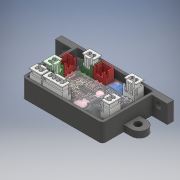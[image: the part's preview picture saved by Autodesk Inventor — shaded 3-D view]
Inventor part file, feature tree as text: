
AUTODESK INVENTOR PART (.ipt)
format: ipt  version: 2017 (Build 210142000, 142)  size: 2,653,696 bytes
history: native  units: mm
features: other x18, sketch x7, extrude x3, fillet x2, hole x2, mirror x1
ambient origin geometry x8: Origin, YZ Plane, XZ Plane, XY Plane, X Axis, Y Axis, Z Axis, Center Point
bodies: Solide10 (feature_tree)
feature tree (33):
  other  "Connecteur jst 2 broches.iam"
  other  "Connecteur jst 4 broches.iam"
  other  "Connecteur jst 2 broches femelle.ipt:1"
  other  "Connecteur JST 2 Broches Male.ipt:1"
  other  "Connecteur jst 4 broches femelle.ipt:1"
  other  "Connecteur JST 4 Broches Male.ipt:1"
  extrude  "Extrusion1"  Depth=71.6mm
  extrude  "Extrusion2"  Depth=4.0mm
  extrude  "Extrusion3"  Depth=35.5mm
  fillet  "Congé1"  Radius=51.5mm
  hole  "Perçage1"  [1 undecoded]
  mirror  "Symétrie1"
  hole  "Perçage2"  [1 undecoded]
  fillet  "Congé2"  Radius=1.7mm
  other  "Epaississement1"
  other  "Décalcomanie1"
  other  "Déplacer des corps1"
  other  "Déplacer des corps2"
  other  "Déplacer des corps3"
  other  "Déplacer des corps4"
  other  "Déplacer des corps5"
  other  "Déplacer des corps7"
  other  "Déplacer des corps8"
  other  "Déplacer des corps9"
  other  "Combiner2"
  sketch  "Esquisse7"
  sketch  "Esquisse1"
  sketch  "Esquisse2"
  sketch  "Esquisse3"
  sketch  "Esquisse4"
  sketch  "Esquisse5"
  sketch  "Esquisse6"
  other  "Image1"
note: 2 required parameter values undecoded (feature->parameter linkage not recoverable at this tier; creation-order binding heuristic only, values carry confidence <= 0.55)
